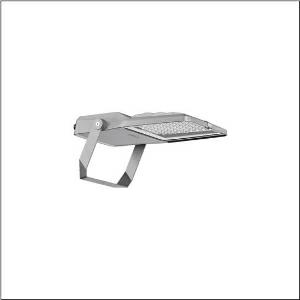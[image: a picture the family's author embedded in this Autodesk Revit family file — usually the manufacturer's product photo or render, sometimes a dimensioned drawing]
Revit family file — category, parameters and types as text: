
# Revit family: floodlight_fl_21_mini___pl33t_5xa7775c2f1a_de84
name_source: partatom
category: Lighting Fixtures
units: mm (PartAtom-declared; Revit-internal decimal feet)

## family parameters
Cut with Voids When Loaded = No
Host = Face
Light Source = No
Part Type = Normal
Room Calculation Point = No
Round Connector Dimension = Use Diameter
Shared = No

## types (1)
- --- (1 x LED, 12050 lm, 89 W, 3000K)
    Apparent Load = 89 VA
    CIE Flux Codes = 26 75 99 100 100
    Color Rendering = 70
    Color Temperature = 3000K
    Default Elevation = 1800 mm
    Description = Floodlight FL 21 mini, floodlight, primary light control with lens, of PMMA, primary optical cover: protective disc, of toughened safety glass, transparent, light distribution: PL33T, light emission: direct distribution, installation type: surface-mounted, LED, High Power LED, rated luminous flux: 12.050lm, luminous efficacy: 135lm/W, light colour: 730, colour temperature: 3000K, control gear: Smart Interface (Zhaga), control: flexible luminous flux parameterisation, time-dependent luminous flux control, constant luminous flux control, overheat protection, pre-setting: logarithmic dimming characteristic, with terminal, 6-pole, mains connection: 220..240V, AC, 50/60Hz, start of lifetime: 89W, end of service life: 94W, reduction: 43W, luminaire housing, of diecast aluminium, powder-coated, SITECO metallic grey (DB 702S), corrosivity category C5 mid according to DIN EN ISO 12944, suitable for swimming pools, chlorine-resistant, sealing non-destructively replaceable, mounting bracket, of steel, galvanised, powder-coated, SITECO metallic grey (DB 702S), Smart Interface above, protection rating (complete): IP66, insulation class (complete): insulation class II (safety insulation), certification: CE, ENEC, VDE, protection symbol: D, impact resistance: IK08, permissible operating ambient temperature: -40..+40°C, permissible operating ambient temperature for outdoor applications: -40..+50°C, standard: DIN EN 12944, LABS conformity tested according to VDMA 24364:2018-05, packaging unit: 1 piece

Light Distribution: PL33T
    Height = 70 mm
    Lamp = 1 x LED
    Lamp Light Flux = 12050 lm
    Lamp Power = 89 W
    Lamp count = 1
    Length = 485 mm
    Luminous efficacy = 135 lm/W
    Manufacturer = Siteco
    ModVariant = No
    Model = 5XA7775C2F1A
    Number of Poles = 1
    OnlyDefault = Yes
    Power Factor = 1
    Product Name = Floodlight FL 21 mini | PL33T
    Product group = floodlight | pylon annexe
    ProductGroupID = 6201
    Protection Class = Protection class II
    Protection Degree = IP 66
    RLX_Detail_Level = 1
    RLX_Emergency_Light_Flux = 0 lm
    RLX_Emergency_Type = 0
    RLX_Emergency_Type_DB = No
    RlxData = <blob elided: 95757 chars, md5=b944b539>
    Socket = socket
    Standby Power = 0 W
    System Light Flux = 12050 lm
    System Power = 89 W
    Type Comments = factory setting: luminous flux: 100 % | dim-lin: 254 | 456 mA
    Type Image = l_1006845.jpg
    URL = http://relux.com
    VarID = @adj_148067
    Voltage = 0 V
    Weight = 0.00 kg
    Width = 337 mm

## geometry (parser evidence)
native form markers: Blend x4, Sweep x11
no freeform markers — native parametric forms only
